# Revit family: Grohe_PlumbingFixture_EuphoriaSystem260_ShowerSystem_274730021
name_source: partatom
category: Plumbing Fixtures
revit_build: Autodesk Revit 2018 (Build: 20190510_1515(x64)
units: mm (PartAtom-declared; Revit-internal decimal feet)

## family parameters
Cut with Voids When Loaded = No
Host = Face
OmniClass Number = 23.45.05.14.17
OmniClass Title = Showers
Part Type = Normal
Room Calculation Point = No
Round Connector Dimension = Use Diameter
Shared = No

## types (1)
- 27473002
    ADACompliant = No
    Assembly Code = D2010710
    AssetType = Fixed
    BIMObjectName = Grohe_PlumbingFixture_EuphoriaSystem260_ShowerSystem_27473002
    CW Connection = Yes
    CWFU = 4.5
    ClassificationName = Uniclass 2015
    ClassificationValue = Pr_40_20_87_76
    ColdWaterConnectionDiameter = 13 mm  [stored 0.0426509 ft]
    Cost = 0 $
    Default Elevation = 0 mm  [stored 0 ft]
    Description = Euphoria system 260 OHM, 9,5l/min
    DocumentationCertificates = www.bimstore.co
    DocumentationInstallationGuide = www.bimstore.co
    DocumentationLiterature = www.bimstore.co
    DocumentationMaintenance = www.bimstore.co
    DocumentationTechnical = www.bimstore.co
    DurationUnit = Years
    Ecojoy = No
    ExpectedLife = 0
    Features = Shower system with single lever for wall mounting Consisting of: horizontal swivable 450 mm projection shower arm exposed single-lever shower mixer  with diverter allows change between: head shower Euphoria 260 (26 457) Rain, SmartRain, Jetwith ball jointrotation angle ± 15°hand shower Euphoria 110 Massage  (27 239 000) 3 spray patterns: Rain, Massage, SmartRain adjustable height via gliding element Silverflex shower hose 1750 mm (28 388 000) GROHE SilkMove 46 mm ceramic cartridge GROHE DreamSpray perfect spray pattern GROHE StarLight chrome finish GROHE SprayDimmer (Stepless  flow rate reduction) GROHE EcoJoy 9.5 l/min flow limiter GROHE FastFixation (upper bracket adjustable) Inner WaterGuide for a longer life SpeedClean anti-limescale system Twistfree preventing the hose from twisting suitable for instantaneous heaters from 18 kW/h minimum flow rate 7 l/min. min. recommended pressure 1 bar professional edition
    Finish = Chrome
    HW Connection = Yes
    HWFU = 4.5
    HotWaterConnectionDiameter = 13 mm  [stored 0.0426509 ft]
    IfcExportAs = IfcPipeFitting
    IfcExportType = IfcPipeFittingType
    Keynote = N13
    LowEmittingMaterial = No
    Manufacturer = Grohe
    ManufacturerName = Grohe
    MasterformatNumber = 01 52 19
    MasterformatTitle = Sanitary Facilities
    Model = Euphoria system 260 OHM, 9,5l/min
    ModelNumber = 27473002
    ModelReference = Euphoria system 260 OHM, 9,5l/min
    NBSDescription = Shower heads
    NBSObjectName = Grohe - Shower heads
    NBSReference = 45-35-70/333
    NominalDepth = 0 mm  [stored 0 ft]
    NominalHeight = 0 mm  [stored 0 ft]
    NominalLength = 0 mm  [stored 0 ft]
    PipeMaterial = GroheLimited-Pipework
    PrimaryMaterial = Grohe-Chrome
    ProductionYear = 2020
    Type Comments = 27473002
    TypeName = 27473002
    URL = www.grohe.com
    WFU = 0
    WarrantyDurationLabor = 0
    WarrantyDurationParts = 0
    WarrantyDurationUnit = Years
    _BSBibleVersion = 16
    _BimSpecGuid = 0
    _CurrentRevision = 1
    _DistributedBy = www.bimstore.co
    _ObjectUserGuide = www.bimstore.co

note: [stored X ft] marks values corroborated as IEEE doubles in the binary element streams (Revit-internal decimal feet)

## geometry (parser evidence)
native form markers: Sweep x1
no freeform markers — native parametric forms only
